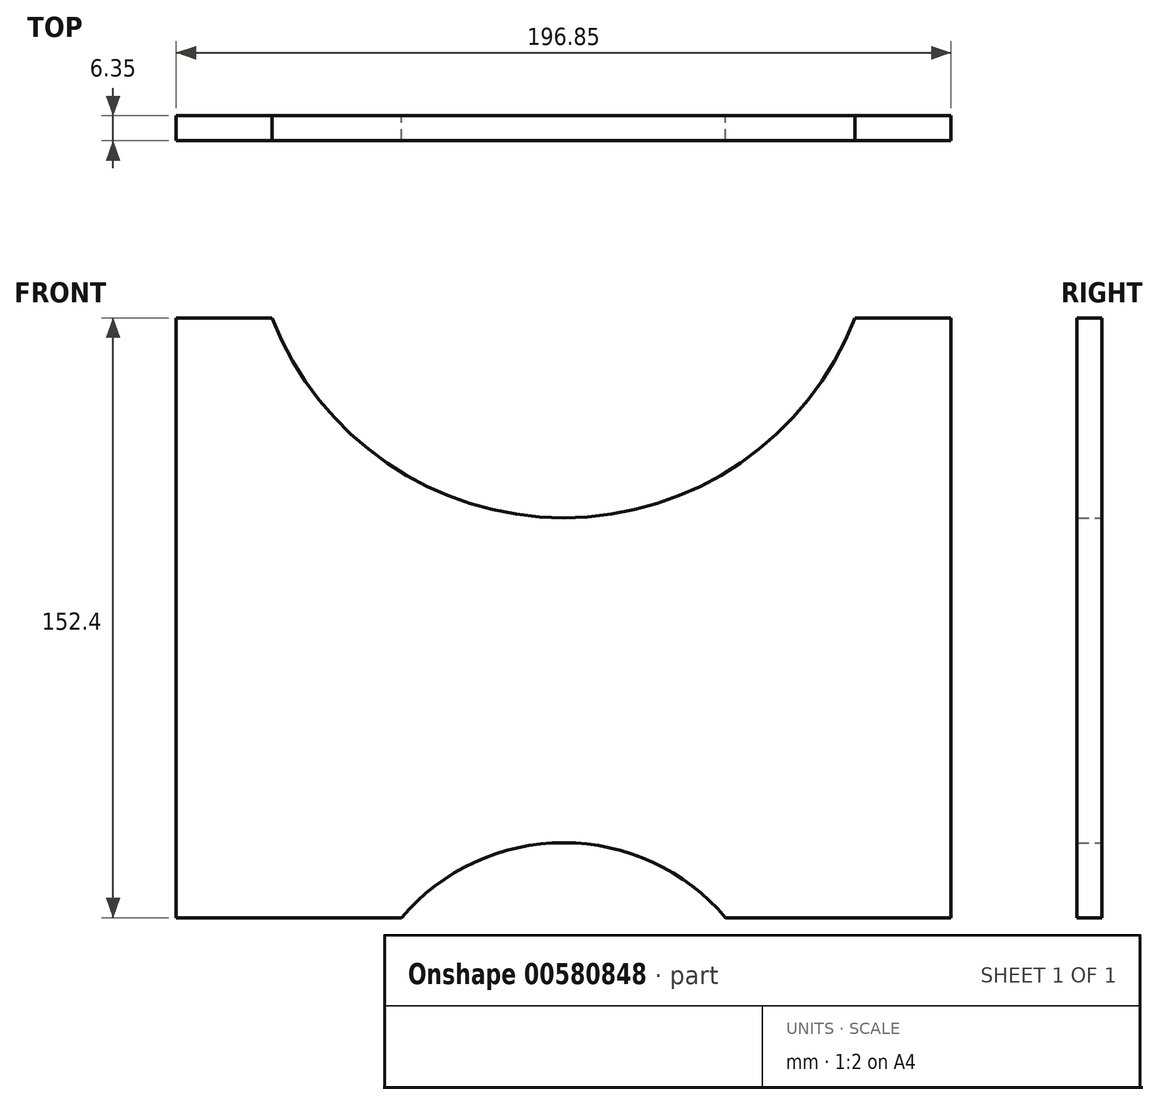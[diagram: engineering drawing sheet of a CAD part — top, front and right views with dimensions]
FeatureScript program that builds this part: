
annotation { "Feature Type Name" : "Feature", "Feature Type Description" : "" }
export const myFeature = defineFeature(function(context is Context, id is Id, definition is map)
    precondition{}
    {
        {
            var Q0;
            Q0=qCreatedBy(makeId("Front.planeOp"),FACE);
            var sketch = newSketch(context, id + "F0", { "sketchPlane" : qUnion([Q0])});
            skLineSegment(sketch, "E0.bottom", {"start": v(-127.2, 52.18) * mm, "end": v(-102.83, 52.18) * mm});
            skLineSegment(sketch, "E0.top", {"start": v(-127.2, -100.22) * mm, "end": v(-69.93, -100.22) * mm});
            skLineSegment(sketch, "E0.left", {"start": v(-127.2, 52.18) * mm, "end": v(-127.2, -100.22) * mm});
            skLineSegment(sketch, "E0.right", {"start": v(69.64, 52.18) * mm, "end": v(69.64, -100.22) * mm});
            skArc(sketch, "E1", {"start": v(-102.83, 52.18) * mm, "mid": v(-28.78, 1.38) * mm, "end": v(45.27, 52.18) * mm});
            skArc(sketch, "E2", {"start": v(12.37, -100.22) * mm, "mid": v(-28.78, -81.17) * mm, "end": v(-69.93, -100.22) * mm});
            skLineSegment(sketch, "E3.trimOffspring", {"start": v(12.37, -100.22) * mm, "end": v(69.64, -100.22) * mm});
            skLineSegment(sketch, "E4.trimOffspring", {"start": v(45.27, 52.18) * mm, "end": v(69.64, 52.18) * mm});
            skSolve(sketch);
        }
        {
            var Q0;
            Q0 = qSketchRegion(id + "F0", true);
            extrude(context, id + "F1", {"entities" : qUnion([Q0]), "depth" : 6.35 * mm, "offsetDistance" : 25.4 * mm});
        }
    });
